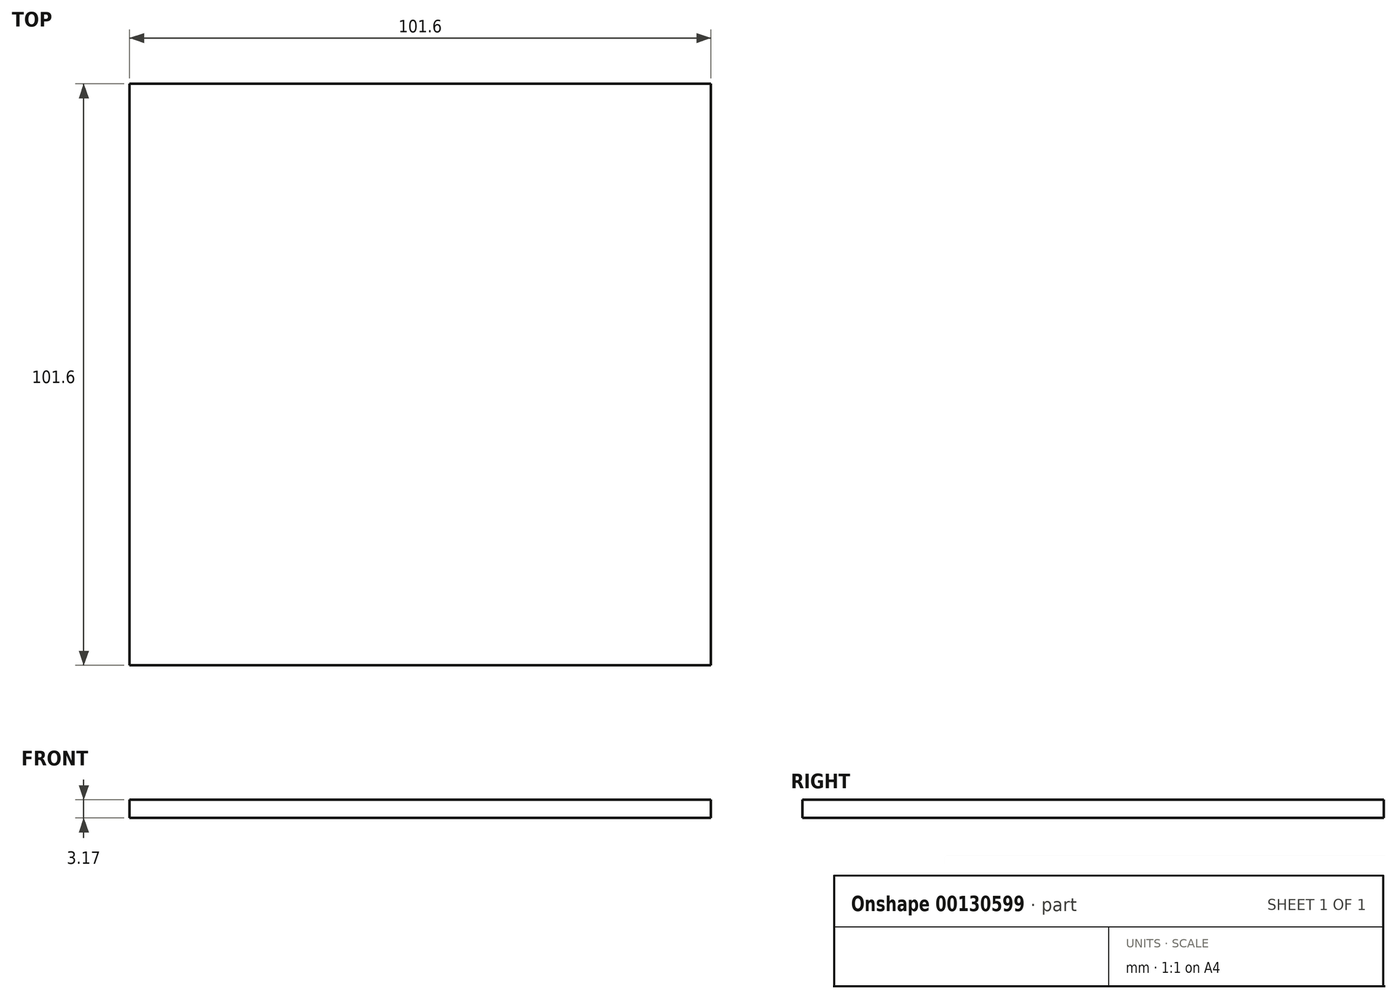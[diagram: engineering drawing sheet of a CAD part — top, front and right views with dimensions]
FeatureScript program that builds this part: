
annotation { "Feature Type Name" : "Feature", "Feature Type Description" : "" }
export const myFeature = defineFeature(function(context is Context, id is Id, definition is map)
    precondition{}
    {
        {
            var Q0;
            Q0=qCreatedBy(makeId("Top.planeOp"),FACE);
            var sketch = newSketch(context, id + "F0", { "sketchPlane" : qUnion([Q0])});
            skLineSegment(sketch, "E0.bottom", {"start": v(-50.8, 50.8) * mm, "end": v(50.8, 50.8) * mm});
            skLineSegment(sketch, "E0.top", {"start": v(-50.8, -50.8) * mm, "end": v(50.8, -50.8) * mm});
            skLineSegment(sketch, "E0.left", {"start": v(-50.8, 50.8) * mm, "end": v(-50.8, -50.8) * mm});
            skLineSegment(sketch, "E0.right", {"start": v(50.8, 50.8) * mm, "end": v(50.8, -50.8) * mm});
            skPoint(sketch, "E0.middle", {"position": v(0, 0) * mm});
            skSolve(sketch);
        }
        {
            var Q0;
            Q0=makeQuery(id+"F0.imprint","IMPRINT",FACE,{"disambiguationData":[TD([[makeQuery(id+"F0.imprint","IMPRINT",EDGE,{"derivedFrom":sQuery(id+"F0.wireOp",EDGE,"E0.bottom")}),-1.0]])]});
            extrude(context, id + "F1", {"entities" : qUnion([Q0]), "depth" : 3.17 * mm});
        }
    });
